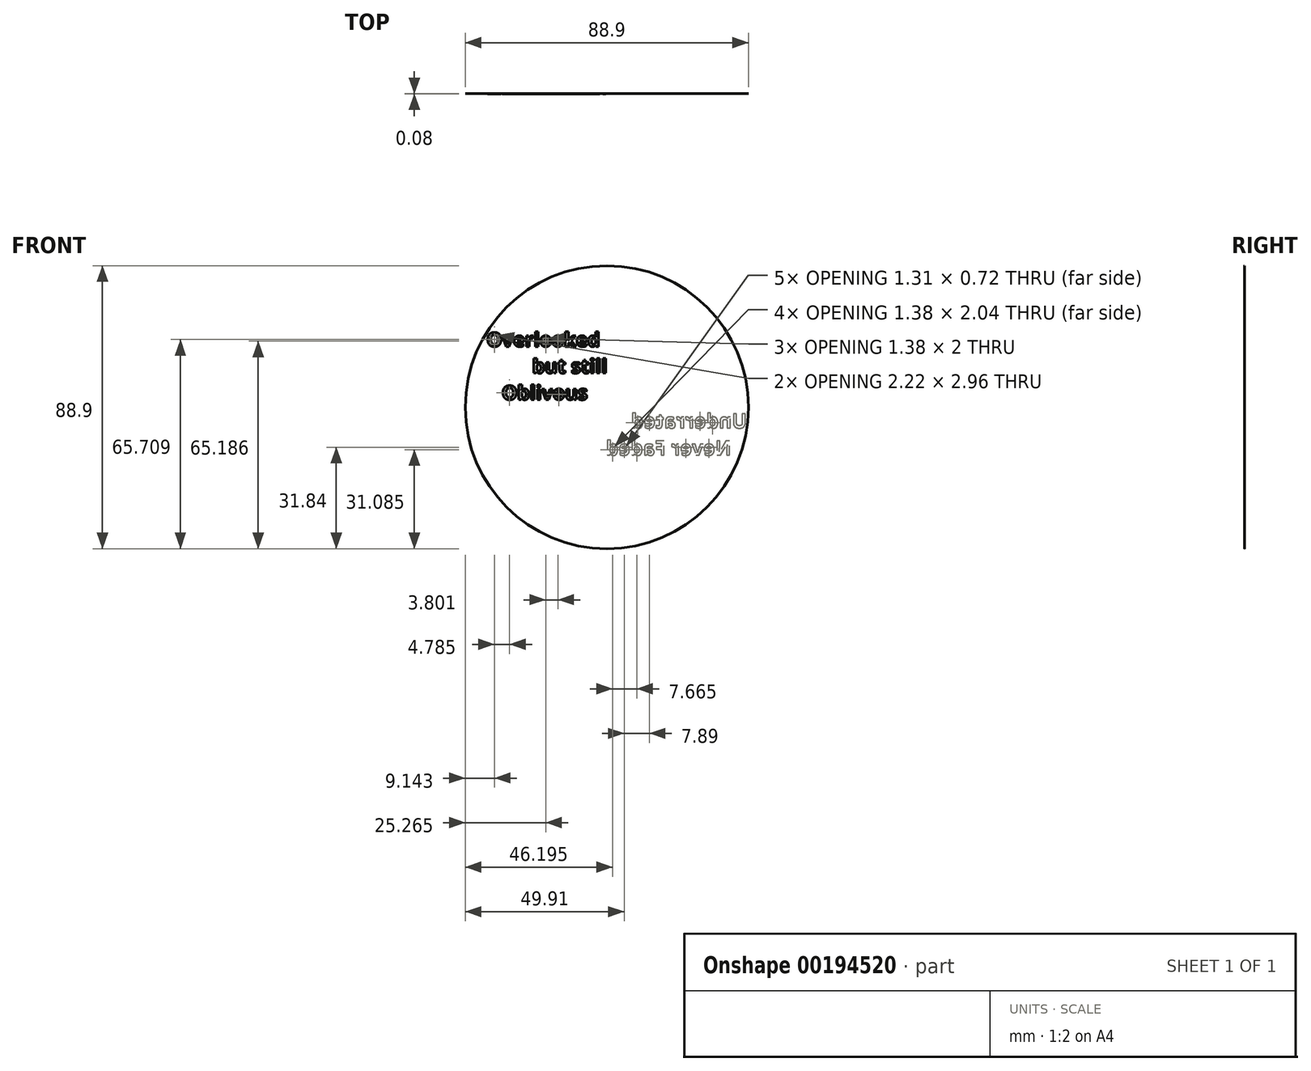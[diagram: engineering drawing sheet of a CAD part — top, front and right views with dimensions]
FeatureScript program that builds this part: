
annotation { "Feature Type Name" : "Feature", "Feature Type Description" : "" }
export const myFeature = defineFeature(function(context is Context, id is Id, definition is map)
    precondition{}
    {
        {
            var Q0;
            Q0=qCreatedBy(makeId("Front.planeOp"),FACE);
            var sketch = newSketch(context, id + "F0", { "sketchPlane" : qUnion([Q0])});
            skCircle(sketch, "E0", {"center": v(0, 0) * mm, "radius": 44.45 * mm});
            skSolve(sketch);
        }
        {
            var Q0;
            Q0=makeQuery(id+"F0.imprint","IMPRINT",FACE,{"disambiguationData":[TD([[makeQuery(id+"F0.imprint","IMPRINT",EDGE,{"derivedFrom":sQuery(id+"F0.wireOp",EDGE,"E0")}),1.0]])]});
            extrude(context, id + "F1", {"entities" : qUnion([Q0]), "depth" : 0.03 * mm});
        }
        {
            var Q0;
            Q0=makeQuery(id+"F1.opExtrude","SWEPT_BODY",BODY,{"disambiguationData":[OSD([sQuery(id+"F0.wireOp",EDGE,"E0")])]});
            var Q1;
            Q1=makeQuery(id+"F1.opExtrude","CAP_EDGE",EDGE,{"disambiguationData":[OSD([sQuery(id+"F0.wireOp",EDGE,"E0")])],"isStart":false});
            circularPattern(context, id + "F2", {"entities" : qUnion([Q0]), "axis" : qUnion([Q1]), "angle" : 360 * degree, "instanceCount" : 4, "equalSpace" : true});
        }
        {
            var Q0;
            Q0=makeQuery(id+"F1.opExtrude","CAP_FACE",FACE,{"disambiguationData":[OSD([sQuery(id+"F0.wireOp",EDGE,"E0")])],"isStart":false});
            var sketch = newSketch(context, id + "F3", { "sketchPlane" : qUnion([Q0])});
            skText(sketch, "E1", { "text": "Overlooked \n         but still\n   Oblivous", "fontName": "OpenSans-Bold.ttf"});
            const initialGuessF3  = {"E1": [-0.03775, 0.01906, 1, 0, 0.00442]};
            skSetInitialGuess(sketch, initialGuessF3);
            skSolve(sketch);
        }
        {
            var Q0;
            Q0 = qSketchRegion(id + "F3", true);
            extrude(context, id + "F4", {"entities" : qUnion([Q0]), "depth" : 0.03 * mm});
        }
        {
            var Q0;
            Q0=makeQuery(id+"F1.opExtrude","CAP_FACE",FACE,{"disambiguationData":[OSD([sQuery(id+"F0.wireOp",EDGE,"E0")])],"isStart":true});
            var sketch = newSketch(context, id + "F5", { "sketchPlane" : qUnion([Q0])});
            skText(sketch, "E2", { "text": "Underrated\n   Never Faded", "fontName": "OpenSans-Bold.ttf"});
            const initialGuessF5  = {"E2": [-0.04396, -0.00655, 1, 0, 0.00451]};
            skSetInitialGuess(sketch, initialGuessF5);
            skSolve(sketch);
        }
        {
            var Q0;
            Q0 = qSketchRegion(id + "F5", true);
            extrude(context, id + "F6", {"entities" : qUnion([Q0]), "depth" : 0.03 * mm});
        }
    });
